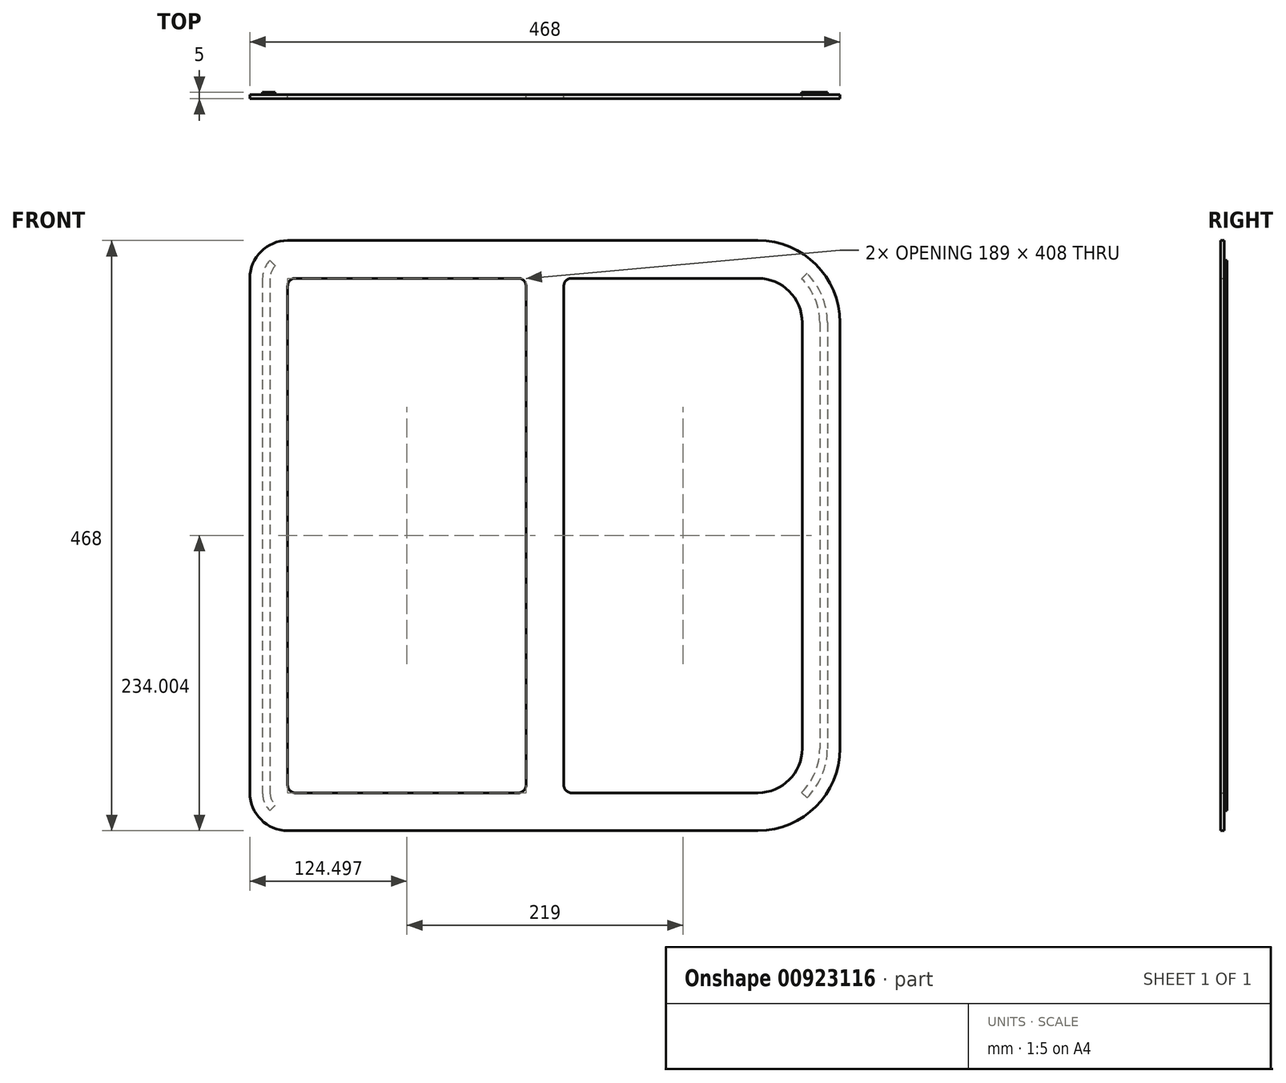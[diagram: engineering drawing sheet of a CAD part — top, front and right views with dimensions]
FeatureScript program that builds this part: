
annotation { "Feature Type Name" : "Feature", "Feature Type Description" : "" }
export const myFeature = defineFeature(function(context is Context, id is Id, definition is map)
    precondition{}
    {
        {
            var Q0;
            Q0=qCreatedBy(makeId("Front.planeOp"),FACE);
            var sketch = newSketch(context, id + "F0", { "sketchPlane" : qUnion([Q0])});
            skLineSegment(sketch, "E0.bottom", {"start": v(-623.97, 419.84) * mm, "end": v(-250.97, 419.84) * mm});
            skLineSegment(sketch, "E0.top", {"start": v(-623.97, -28.16) * mm, "end": v(-250.97, -28.16) * mm});
            skLineSegment(sketch, "E0.left", {"start": v(-643.97, 399.84) * mm, "end": v(-643.97, -8.16) * mm});
            skLineSegment(sketch, "E0.right", {"start": v(-195.97, 364.84) * mm, "end": v(-195.97, 26.84) * mm});
            skArc(sketch, "E1.filletArc", {"start": v(-623.97, 419.84) * mm, "mid": v(-638.12, 413.99) * mm, "end": v(-643.97, 399.84) * mm});
            skPoint(sketch, "E2.visualSharp", {"position": v(-643.97, -28.16) * mm});
            skArc(sketch, "E2.filletArc", {"start": v(-643.97, -8.16) * mm, "mid": v(-638.12, -22.3) * mm, "end": v(-623.97, -28.16) * mm});
            skPoint(sketch, "E3.visualSharp", {"position": v(-195.97, 419.84) * mm});
            skArc(sketch, "E3.filletArc", {"start": v(-195.97, 364.84) * mm, "mid": v(-212.08, 403.73) * mm, "end": v(-250.97, 419.84) * mm});
            skPoint(sketch, "E4.visualSharp", {"position": v(-195.97, -28.16) * mm});
            skArc(sketch, "E4.filletArc", {"start": v(-250.97, -28.16) * mm, "mid": v(-212.08, -12.05) * mm, "end": v(-195.97, 26.84) * mm});
            skArc(sketch, "E5.0", {"start": v(-185.97, 364.84) * mm, "mid": v(-205.01, 410.8) * mm, "end": v(-250.97, 429.84) * mm});
            skArc(sketch, "E6.0", {"start": v(-653.97, -8.16) * mm, "mid": v(-645.19, -29.37) * mm, "end": v(-623.97, -38.16) * mm});
            skLineSegment(sketch, "E7.0", {"start": v(-653.97, 399.84) * mm, "end": v(-653.97, -8.16) * mm});
            skLineSegment(sketch, "E8.0", {"start": v(-623.97, -38.16) * mm, "end": v(-250.97, -38.16) * mm});
            skArc(sketch, "E9.2", {"start": v(-250.97, -38.16) * mm, "mid": v(-205.01, -19.12) * mm, "end": v(-185.97, 26.84) * mm});
            skLineSegment(sketch, "E9.4", {"start": v(-185.97, 364.84) * mm, "end": v(-185.97, 26.84) * mm});
            skLineSegment(sketch, "E9.6", {"start": v(-623.97, 429.84) * mm, "end": v(-250.97, 429.84) * mm});
            skArc(sketch, "E9.7", {"start": v(-623.97, 429.84) * mm, "mid": v(-645.19, 421.06) * mm, "end": v(-653.97, 399.84) * mm});
            skArc(sketch, "E10.0", {"start": v(-637.97, -8.16) * mm, "mid": v(-633.87, -18.06) * mm, "end": v(-623.97, -22.16) * mm});
            skLineSegment(sketch, "E10.1", {"start": v(-637.97, 399.84) * mm, "end": v(-637.97, -8.16) * mm});
            skLineSegment(sketch, "E10.2", {"start": v(-623.97, -22.16) * mm, "end": v(-428.97, -22.16) * mm});
            skArc(sketch, "E10.3", {"start": v(-623.97, 413.84) * mm, "mid": v(-633.87, 409.74) * mm, "end": v(-637.97, 399.84) * mm});
            skArc(sketch, "E10.4", {"start": v(-250.97, -22.16) * mm, "mid": v(-216.32, -7.8) * mm, "end": v(-201.97, 26.84) * mm});
            skLineSegment(sketch, "E10.5", {"start": v(-201.97, 364.84) * mm, "end": v(-201.97, 26.84) * mm});
            skArc(sketch, "E10.6", {"start": v(-201.97, 364.84) * mm, "mid": v(-216.32, 399.5) * mm, "end": v(-250.97, 413.84) * mm});
            skLineSegment(sketch, "E10.7", {"start": v(-623.97, 413.84) * mm, "end": v(-428.97, 413.84) * mm});
            skLineSegment(sketch, "E11.0", {"start": v(-623.97, 393.84) * mm, "end": v(-623.97, -2.16) * mm});
            skLineSegment(sketch, "E11.1", {"start": v(-623.97, 399.84) * mm, "end": v(-623.97, 399.84) * mm});
            skLineSegment(sketch, "E11.3", {"start": v(-617.97, 399.84) * mm, "end": v(-440.97, 399.84) * mm});
            skLineSegment(sketch, "E11.4", {"start": v(-617.97, -8.16) * mm, "end": v(-440.97, -8.16) * mm});
            skArc(sketch, "E12.filletArc", {"start": v(-623.97, -2.16) * mm, "mid": v(-622.22, -6.4) * mm, "end": v(-617.97, -8.16) * mm});
            skArc(sketch, "E13.filletArc", {"start": v(-617.97, 399.84) * mm, "mid": v(-622.22, 398.09) * mm, "end": v(-623.97, 393.84) * mm});
            skLineSegment(sketch, "E14", {"start": v(-201.97, 195.84) * mm, "end": v(-195.97, 195.84) * mm});
            skLineSegment(sketch, "E15", {"start": v(-643.97, 195.84) * mm, "end": v(-637.97, 195.84) * mm});
            skLineSegment(sketch, "E16", {"start": v(-638.12, -22.3) * mm, "end": v(-633.87, -18.06) * mm});
            skLineSegment(sketch, "E17", {"start": v(-212.08, -12.05) * mm, "end": v(-216.32, -7.8) * mm});
            skLineSegment(sketch, "E18", {"start": v(-212.08, 403.73) * mm, "end": v(-216.32, 399.5) * mm});
            skLineSegment(sketch, "E19", {"start": v(-633.87, 409.74) * mm, "end": v(-637.97, 414.13) * mm});
            skLineSegment(sketch, "E20.trimOffspring", {"start": v(-398.97, 399.84) * mm, "end": v(-250.97, 399.84) * mm});
            skLineSegment(sketch, "E21.trimOffspring", {"start": v(-398.97, -8.16) * mm, "end": v(-250.97, -8.16) * mm});
            skPoint(sketch, "E22.end.orphan", {"position": v(-434.47, -8.16) * mm});
            skPoint(sketch, "E22.start.orphan", {"position": v(-434.47, 399.84) * mm});
            skPoint(sketch, "E23.visualSharp", {"position": v(-448.47, 399.84) * mm});
            skPoint(sketch, "E24.visualSharp", {"position": v(-448.47, -8.16) * mm});
            skPoint(sketch, "E25.visualSharp", {"position": v(-419.47, -8.16) * mm});
            skPoint(sketch, "E26.visualSharp", {"position": v(-419.47, 399.84) * mm});
            skLineSegment(sketch, "E27", {"start": v(-404.97, 393.84) * mm, "end": v(-404.97, -2.16) * mm});
            skLineSegment(sketch, "E28.0", {"start": v(-434.97, 393.84) * mm, "end": v(-434.97, -2.16) * mm});
            skPoint(sketch, "E29.visualSharp", {"position": v(-434.97, 399.84) * mm});
            skArc(sketch, "E29.filletArc", {"start": v(-434.97, 393.84) * mm, "mid": v(-436.73, 398.09) * mm, "end": v(-440.97, 399.84) * mm});
            skPoint(sketch, "E30.visualSharp", {"position": v(-434.97, -8.16) * mm});
            skArc(sketch, "E30.filletArc", {"start": v(-440.97, -8.16) * mm, "mid": v(-436.73, -6.4) * mm, "end": v(-434.97, -2.16) * mm});
            skPoint(sketch, "E31.visualSharp", {"position": v(-404.97, -8.16) * mm});
            skArc(sketch, "E31.filletArc", {"start": v(-404.97, -2.16) * mm, "mid": v(-403.22, -6.4) * mm, "end": v(-398.97, -8.16) * mm});
            skPoint(sketch, "E32.visualSharp", {"position": v(-404.97, 399.84) * mm});
            skArc(sketch, "E32.filletArc", {"start": v(-398.97, 399.84) * mm, "mid": v(-403.22, 398.09) * mm, "end": v(-404.97, 393.84) * mm});
            skArc(sketch, "E33.0", {"start": v(-215.97, 364.84) * mm, "mid": v(-226.22, 389.6) * mm, "end": v(-250.97, 399.84) * mm});
            skLineSegment(sketch, "E33.1", {"start": v(-215.97, 364.84) * mm, "end": v(-215.97, 26.84) * mm});
            skArc(sketch, "E33.2", {"start": v(-250.97, -8.16) * mm, "mid": v(-226.22, 2.1) * mm, "end": v(-215.97, 26.84) * mm});
            skLineSegment(sketch, "E34", {"start": v(-416.97, 407.84) * mm, "end": v(-416.97, -16.16) * mm});
            skLineSegment(sketch, "E35", {"start": v(-422.97, 407.84) * mm, "end": v(-422.97, -16.16) * mm});
            skLineSegment(sketch, "E36.trimOffspring", {"start": v(-410.97, 413.84) * mm, "end": v(-250.97, 413.84) * mm});
            skLineSegment(sketch, "E37.trimOffspring", {"start": v(-410.97, -22.16) * mm, "end": v(-250.97, -22.16) * mm});
            skPoint(sketch, "E38.visualSharp", {"position": v(-416.97, -22.16) * mm});
            skArc(sketch, "E38.filletArc", {"start": v(-416.97, -16.16) * mm, "mid": v(-415.22, -20.4) * mm, "end": v(-410.97, -22.16) * mm});
            skPoint(sketch, "E39.visualSharp", {"position": v(-422.97, -22.16) * mm});
            skArc(sketch, "E39.filletArc", {"start": v(-428.97, -22.16) * mm, "mid": v(-424.73, -20.4) * mm, "end": v(-422.97, -16.16) * mm});
            skPoint(sketch, "E40.visualSharp", {"position": v(-416.97, 413.84) * mm});
            skArc(sketch, "E40.filletArc", {"start": v(-410.97, 413.84) * mm, "mid": v(-415.22, 412.09) * mm, "end": v(-416.97, 407.84) * mm});
            skPoint(sketch, "E41.visualSharp", {"position": v(-422.97, 413.84) * mm});
            skArc(sketch, "E41.filletArc", {"start": v(-422.97, 407.84) * mm, "mid": v(-424.73, 412.09) * mm, "end": v(-428.97, 413.84) * mm});
            skSolve(sketch);
        }
        {
            var Q0;
            Q0=makeQuery(id+"F0.imprint","IMPRINT",FACE,{"disambiguationData":[TD([[makeQuery(id+"F0.imprint","IMPRINT",EDGE,{"derivedFrom":sQuery(id+"F0.wireOp",EDGE,"E10.0")}),1.0]])]});
            var Q1;
            Q1=makeQuery(id+"F0.imprint","IMPRINT",FACE,{"disambiguationData":[TD([[makeQuery(id+"F0.imprint","IMPRINT",EDGE,{"derivedFrom":sQuery(id+"F0.wireOp",EDGE,"E0.bottom")}),1.0]])]});
            var Q2;
            Q2=makeQuery(id+"F0.imprint","IMPRINT",FACE,{"disambiguationData":[TD([[makeQuery(id+"F0.imprint","IMPRINT",EDGE,{"derivedFrom":sQuery(id+"F0.wireOp",EDGE,"E0.bottom")}),-1.0]])]});
            var Q3;
            {var subQ3=sQuery(id+"F0.wireOp",EDGE,"E14");Q3=makeQuery(id+"F0.imprint","IMPRINT",FACE,{"disambiguationData":[TD([[makeQuery(id+"F0.imprint","IMPRINT",EDGE,{"derivedFrom":subQ3}),1.0]])]});}
            var Q4;
            {var subQ4=sQuery(id+"F0.wireOp",EDGE,"E14");Q4=makeQuery(id+"F0.imprint","IMPRINT",FACE,{"disambiguationData":[TD([[makeQuery(id+"F0.imprint","IMPRINT",EDGE,{"derivedFrom":subQ4}),-1.0]])]});}
            var Q5;
            {var subQ4=sQuery(id+"F0.wireOp",EDGE,"dK6DxnXH-vQra-UNX6-OGhK-5l2VkbHkdnDd");Q5=makeQuery(id+"F0.imprint","IMPRINT",FACE,{"disambiguationData":[TD([[makeQuery(id+"F0.imprint","IMPRINT",EDGE,{"derivedFrom":subQ4}),-1.0]])]});}
            var Q6;
            {var subQ3=sQuery(id+"F0.wireOp",EDGE,"dK6DxnXH-vQra-UNX6-OGhK-5l2VkbHkdnDd");Q6=makeQuery(id+"F0.imprint","IMPRINT",FACE,{"disambiguationData":[TD([[makeQuery(id+"F0.imprint","IMPRINT",EDGE,{"derivedFrom":subQ3}),1.0]])]});}
            var Q7;
            {var subQ3=sQuery(id+"F0.wireOp",EDGE,"E15");Q7=makeQuery(id+"F0.imprint","IMPRINT",FACE,{"disambiguationData":[TD([[makeQuery(id+"F0.imprint","IMPRINT",EDGE,{"derivedFrom":subQ3}),-1.0]])]});}
            var Q8;
            {var subQ7=sQuery(id+"F0.wireOp",EDGE,"E15");Q8=makeQuery(id+"F0.imprint","IMPRINT",FACE,{"disambiguationData":[TD([[makeQuery(id+"F0.imprint","IMPRINT",EDGE,{"derivedFrom":subQ7}),1.0]])]});}
            var Q9;
            Q9=makeQuery(id+"F0.imprint","IMPRINT",FACE,{"disambiguationData":[TD([[makeQuery(id+"F0.imprint","IMPRINT",EDGE,{"derivedFrom":sQuery(id+"F0.wireOp",EDGE,"E20.trimOffspring")}),1.0]])]});
            extrude(context, id + "F1", {"entities" : qUnion([Q0, Q1, Q2, Q3, Q4, Q5, Q6, Q7, Q8, Q9]), "depth" : 3 * mm, "offsetDistance" : 25 * mm});
        }
        {
            var Q0;
            {var subQ3=sQuery(id+"F0.wireOp",EDGE,"lzmjhSjL-x4lb-fKSA-rnPL-Ya5awNTLKQy0");Q0=makeQuery(id+"F0.imprint","IMPRINT",FACE,{"disambiguationData":[TD([[makeQuery(id+"F0.imprint","IMPRINT",EDGE,{"derivedFrom":subQ3}),1.0]])]});}
            var Q1;
            {var subQ3=sQuery(id+"F0.wireOp",EDGE,"E14");Q1=makeQuery(id+"F0.imprint","IMPRINT",FACE,{"disambiguationData":[TD([[makeQuery(id+"F0.imprint","IMPRINT",EDGE,{"derivedFrom":subQ3}),1.0]])]});}
            var Q2;
            {var subQ4=sQuery(id+"F0.wireOp",EDGE,"E14");Q2=makeQuery(id+"F0.imprint","IMPRINT",FACE,{"disambiguationData":[TD([[makeQuery(id+"F0.imprint","IMPRINT",EDGE,{"derivedFrom":subQ4}),-1.0]])]});}
            var Q3;
            {var subQ4=sQuery(id+"F0.wireOp",EDGE,"dK6DxnXH-vQra-UNX6-OGhK-5l2VkbHkdnDd");Q3=makeQuery(id+"F0.imprint","IMPRINT",FACE,{"disambiguationData":[TD([[makeQuery(id+"F0.imprint","IMPRINT",EDGE,{"derivedFrom":subQ4}),-1.0]])]});}
            var Q4;
            {var subQ3=sQuery(id+"F0.wireOp",EDGE,"dK6DxnXH-vQra-UNX6-OGhK-5l2VkbHkdnDd");Q4=makeQuery(id+"F0.imprint","IMPRINT",FACE,{"disambiguationData":[TD([[makeQuery(id+"F0.imprint","IMPRINT",EDGE,{"derivedFrom":subQ3}),1.0]])]});}
            var Q5;
            {var subQ3=sQuery(id+"F0.wireOp",EDGE,"E15");Q5=makeQuery(id+"F0.imprint","IMPRINT",FACE,{"disambiguationData":[TD([[makeQuery(id+"F0.imprint","IMPRINT",EDGE,{"derivedFrom":subQ3}),-1.0]])]});}
            var Q6;
            {var subQ7=sQuery(id+"F0.wireOp",EDGE,"E15");Q6=makeQuery(id+"F0.imprint","IMPRINT",FACE,{"disambiguationData":[TD([[makeQuery(id+"F0.imprint","IMPRINT",EDGE,{"derivedFrom":subQ7}),1.0]])]});}
            var Q7;
            {var subQ3=sQuery(id+"F0.wireOp",EDGE,"lzmjhSjL-x4lb-fKSA-rnPL-Ya5awNTLKQy0");Q7=makeQuery(id+"F0.imprint","IMPRINT",FACE,{"disambiguationData":[TD([[makeQuery(id+"F0.imprint","IMPRINT",EDGE,{"derivedFrom":subQ3}),-1.0]])]});}
            extrude(context, id + "F2", {"entities" : qUnion([Q0, Q1, Q2, Q3, Q4, Q5, Q6, Q7]), "operationType" : NewBodyOperationType.ADD, "oppositeDirection" : true, "depth" : 2 * mm, "offsetDistance" : 25 * mm});
        }
    });
